# Revit family: 205_SLCU50 600
name_source: partatom
category: Duct Accessories
revit_build: Autodesk Revit 2018 (Build: 20170223_1515(x64)
units: mm (PartAtom-declared; Revit-internal decimal feet)

## family parameters
Always vertical = Yes
Cut with Voids When Loaded = No
Part Type = Breaks Into
Round Connector Dimension = Use Diameter
Shared = No
Work Plane-Based = No

## types (3) — shared parameters
CAT0 = Yes
Description = Silencer steel 0,6m
H2D = 210 mm
L1 = 10 mm  [stored 0.0328084 ft]
L1__ve = -10 mm  [stored -0.0328084 ft]
L2 = 20 mm  [stored 0.0656168 ft]
L22 = 300 mm  [stored 0.984252 ft]
L2D = 600 mm
LL = 540 mm  [stored 1.77165 ft]
Manufacturer = Flexit
QmdConnectorList = 201;D;202;D
URL = www.flexit.no
W2D = 210 mm
magiPartTypeId = 205
magiProductFamilyId = SLCU50 600

## per-type parameters (varying)
| type | D | D1 | D2 | R | magiProductId |
| 100-12521 | 100 mm | 210 mm | 185 mm | 50 mm  [stored 0.164042 ft] | SLCU 100 600 50 |
| 125-12522 | 125 mm | 235 mm | 207 mm | 63 mm | SLCU 125 600 50 |
| 160-12523 | 160 mm | 270 mm  [stored 0.885827 ft] | 238 mm | 80 mm  [stored 0.262467 ft] | SLCU 160 600 50 |

note: column(s) folded — value = type name in every type: MC Product Code

note: [stored X ft] marks values corroborated as IEEE doubles in the binary element streams (Revit-internal decimal feet)

## geometry (parser evidence)
native form markers: Sweep x2
no freeform markers — native parametric forms only
